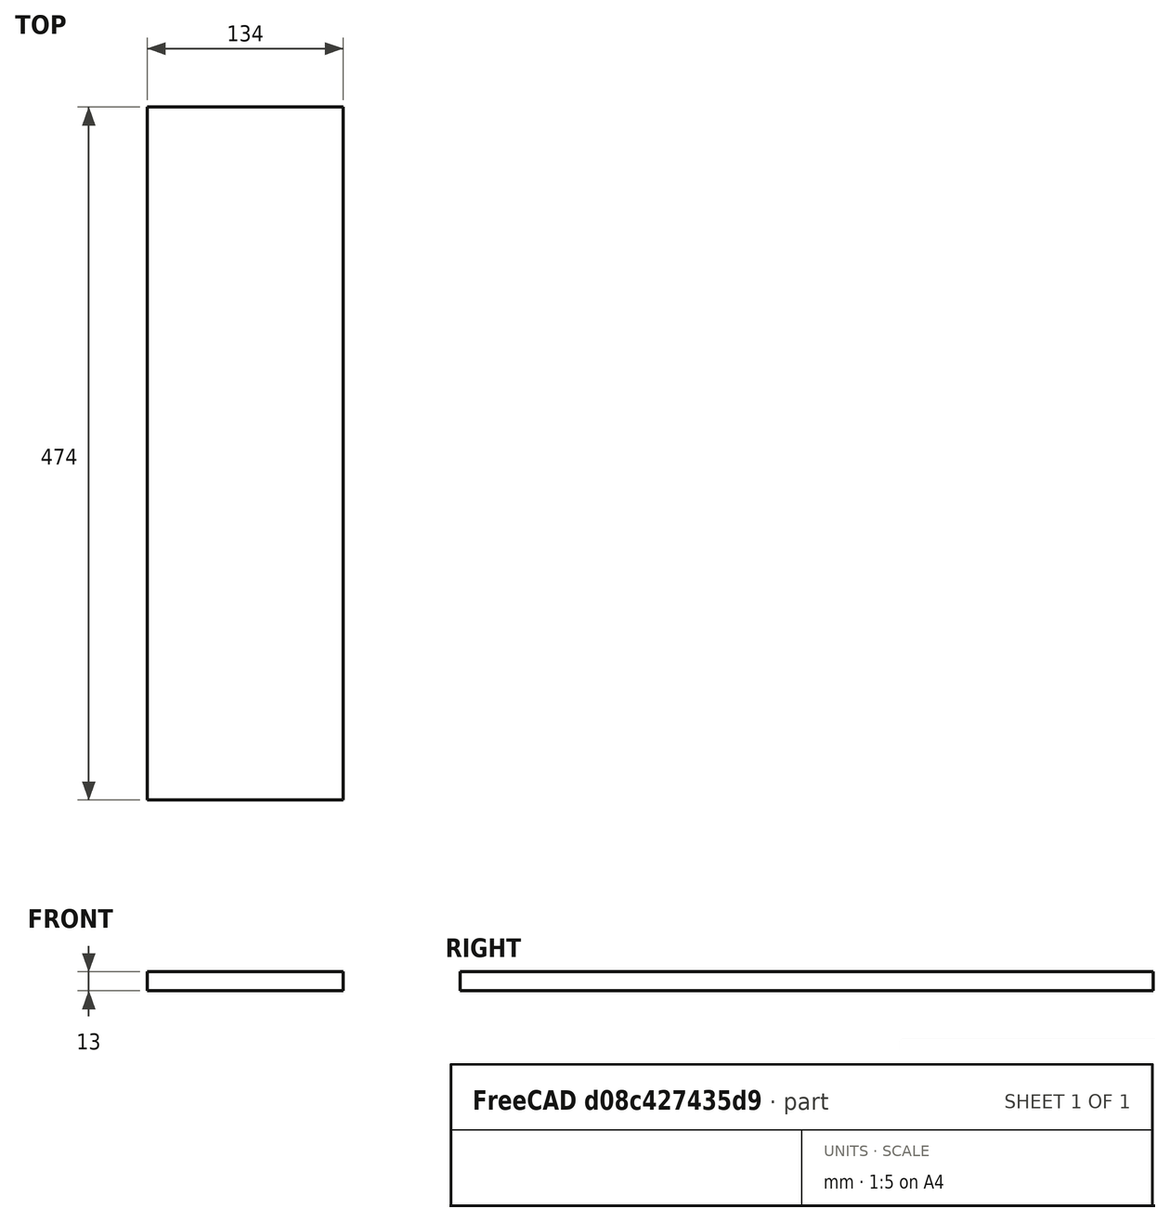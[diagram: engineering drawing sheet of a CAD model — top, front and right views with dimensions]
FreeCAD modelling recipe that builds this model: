
FCSTD DOCUMENT  (FreeCAD 0.18R14555 (Git shallow))
Label: 1001_keyboard_floor_16_
License: All rights reserved
LicenseURL: http://en.wikipedia.org/wiki/All_rights_reserved
objects: Sketcher::SketchObject×1, PartDesign::Pad×1, PartDesign::Body×1, Spreadsheet::Sheet×1
note: 4 computed .brp shape members not serialized (recipe doc carries the construction recipe); baked Part::Feature solids carry a one-line shape summary decoded from their .brp

FEATURE [Sketcher::SketchObject] Sketch
  MapMode = 5
  Support = -> [XY_Plane]
  expr: Constraints[6] = xls.k_d
  expr: Constraints[5] = xls.k_w
  sketch-geometry (5):
    g0: LineSegment StartX=1e-16 StartY=474 StartZ=0 EndX=134 EndY=474 EndZ=0
    g1: LineSegment StartX=134 StartY=474 StartZ=0 EndX=134 EndY=0 EndZ=0
    g2: LineSegment StartX=134 StartY=0 StartZ=0 EndX=0 EndY=0 EndZ=0
    g3: LineSegment StartX=1e-16 StartY=0 StartZ=0 EndX=1e-16 EndY=237 EndZ=0
    g4: LineSegment StartX=1e-16 StartY=237 StartZ=0 EndX=1e-16 EndY=474 EndZ=0
  constraints (14):
    c: Coincident(g0,g1)
    c: Coincident(g1,g2)
    c: Horizontal(g0)
    c: Horizontal(g2)
    c: Vertical(g1)
    c: DistanceY(g1,g1) = 474
    c: DistanceX(g0,g0) = 134
    c: Coincident(g3,g2)
    c: Coincident(g4,g0)
    c: Equal(g3,g4)
    c: Vertical(g4)
    c: Vertical(g3)
    c: Coincident(g3,g4)
    c: Coincident(g2,g-1)
FEATURE [PartDesign::Pad] Pad
  Length = 13
  Length2 = 100
  Profile = -> Sketch
  Type = 0
  expr: Length = xls.k_t_0
FEATURE [PartDesign::Body] Body
  Group = -> [Sketch,Pad]
  Origin = -> Origin
  Tip = -> Pad
FEATURE [Spreadsheet::Sheet] Spreadsheet  label="xls"
  cells = B1=INHERITED; B2=Thickness Front; D2=16; E2=mm; B5=FLOOR; B6=Thickness; C6=k_t_0; D6(k_t_0)=13; E6=mm; B7=Width Nominal; D7=500; B8=Width; C8=k_w; D8(k_w)==D7 - D6 - D6; E8=mm; B9=Deapth Nominal; D9=150; B10=Deapth; C10=k_d; D10(k_d)==+D9 - D2; E10=mm
